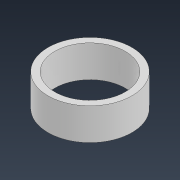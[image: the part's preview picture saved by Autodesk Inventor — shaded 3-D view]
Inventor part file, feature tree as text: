
AUTODESK INVENTOR PART (.ipt)
format: ipt  version: 2022 (Build 260153000, 153)  size: 83,968 bytes
history: native  units: mm
features: extrude x1, sketch x1
ambient origin geometry x8: Origin, YZ Plane, XZ Plane, XY Plane, X Axis, Y Axis, Z Axis, Center Point
bodies: Solid1 (feature_tree)
feature tree (2):
  extrude  "Extrusion1"  Depth=19.0mm
  sketch  "Sketch1"  dims[d0=50.0mm d1=42.0mm d2=19.0mm d3=0.0mm]
